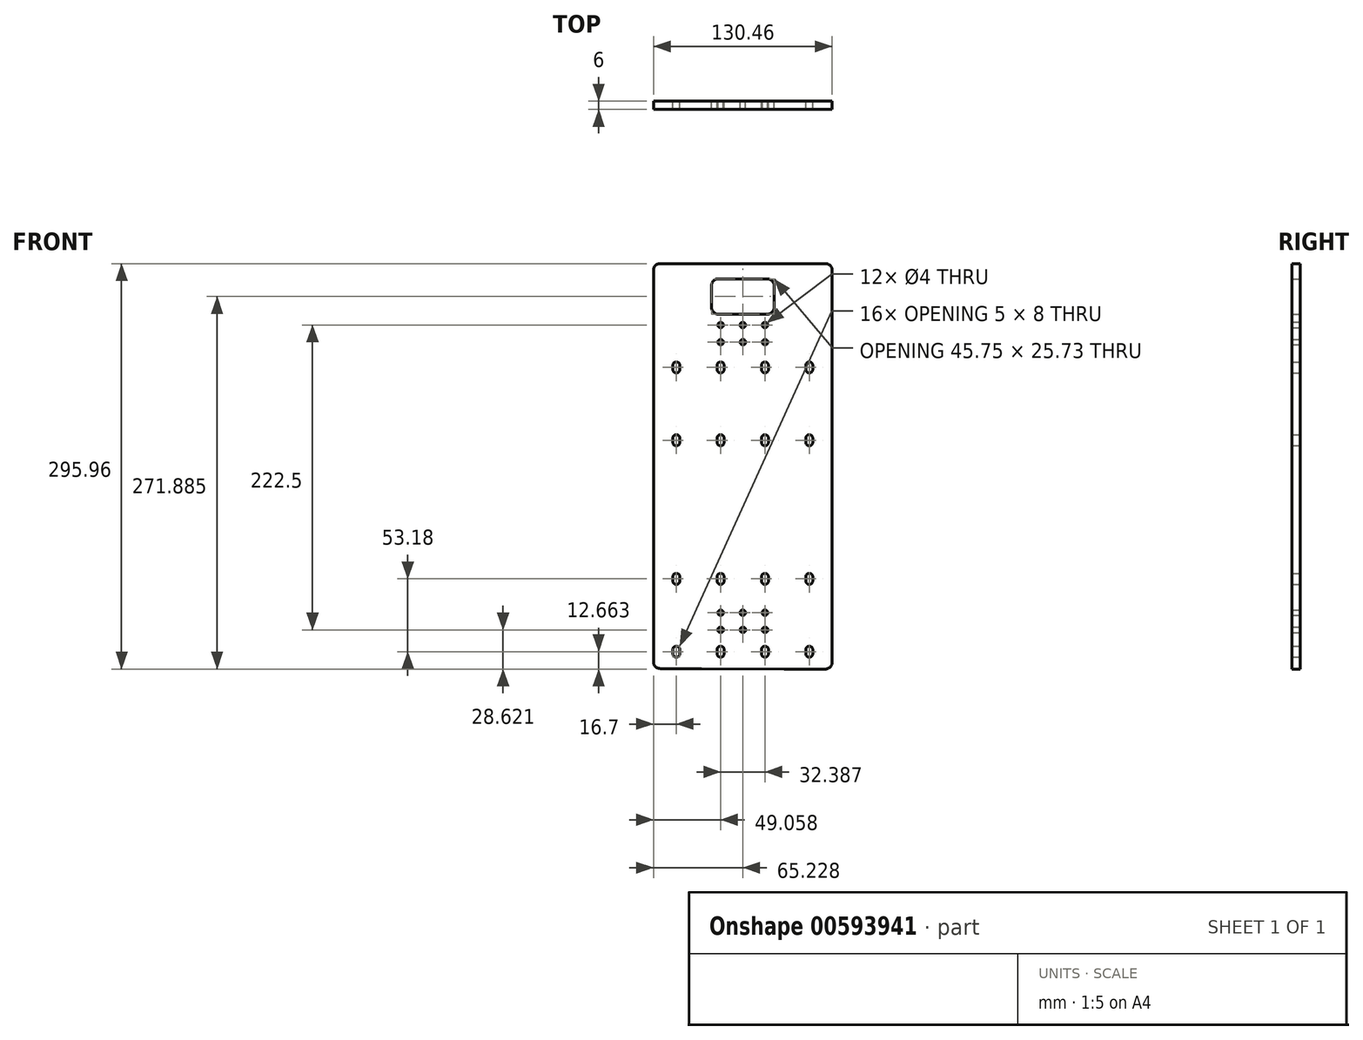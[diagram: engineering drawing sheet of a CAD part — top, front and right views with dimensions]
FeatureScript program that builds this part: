
annotation { "Feature Type Name" : "Feature", "Feature Type Description" : "" }
export const myFeature = defineFeature(function(context is Context, id is Id, definition is map)
    precondition{}
    {
        {
            var Q0;
            Q0=qCreatedBy(makeId("Front.planeOp"),FACE);
            var sketch = newSketch(context, id + "F0", { "sketchPlane" : qUnion([Q0])});
            skLineSegment(sketch, "E0.bottom", {"start": v(-82.55, 112.46) * mm, "end": v(-203.01, 112.46) * mm});
            skCircle(sketch, "E1", {"center": v(-142.78, 106.21) * mm, "radius": 2 * mm});
            skPoint(sketch, "E1.centerSnap0", {"position": v(-142.78, 112.46) * mm});
            skPoint(sketch, "E1.centerSnap1", {"position": v(-97.78, 99.96) * mm});
            skCircle(sketch, "E2.1.0.0", {"center": v(-126.61, 106.21) * mm, "radius": 2 * mm});
            skLineSegment(sketch, "E2.direction1", {"start": v(-142.78, 106.21) * mm, "end": v(-126.61, 106.21) * mm, "construction": true});
            skCircle(sketch, "E3.1.0.0", {"center": v(-158.95, 106.21) * mm, "radius": 2 * mm});
            skLineSegment(sketch, "E3.direction1", {"start": v(-142.78, 106.21) * mm, "end": v(-158.95, 106.21) * mm, "construction": true});
            skPoint(sketch, "E4", {"position": v(-97.78, 112.46) * mm});
            skCircle(sketch, "E5.2.1.0", {"center": v(-126.56, 93.71) * mm, "radius": 2 * mm});
            skCircle(sketch, "E5.2.1.1", {"center": v(-142.73, 93.71) * mm, "radius": 2 * mm});
            skCircle(sketch, "E5.2.1.2", {"center": v(-158.95, 93.71) * mm, "radius": 2 * mm});
            skLineSegment(sketch, "E5.direction1", {"start": v(-149.11, 106.21) * mm, "end": v(-149.11, 106.21) * mm});
            skLineSegment(sketch, "E5.direction2", {"start": v(-126.61, 106.21) * mm, "end": v(-126.56, 93.71) * mm, "construction": true});
            skLineSegment(sketch, "E6.bottom", {"start": v(-94.18, 79.25) * mm, "end": v(-94.4, 79.25) * mm});
            skLineSegment(sketch, "E6.top", {"start": v(-94.18, 71.25) * mm, "end": v(-94.4, 71.25) * mm});
            skLineSegment(sketch, "E6.left", {"start": v(-91.8, 76.87) * mm, "end": v(-91.8, 73.64) * mm});
            skLineSegment(sketch, "E6.right", {"start": v(-96.8, 76.87) * mm, "end": v(-96.8, 73.64) * mm});
            skPoint(sketch, "E7.visualSharp", {"position": v(-91.8, 79.25) * mm});
            skArc(sketch, "E7.filletArc", {"start": v(-91.8, 76.87) * mm, "mid": v(-92.49, 78.55) * mm, "end": v(-94.18, 79.25) * mm});
            skPoint(sketch, "E8.visualSharp", {"position": v(-91.8, 71.25) * mm});
            skArc(sketch, "E8.filletArc", {"start": v(-94.18, 71.25) * mm, "mid": v(-92.49, 71.95) * mm, "end": v(-91.8, 73.64) * mm});
            skPoint(sketch, "E9.visualSharp", {"position": v(-96.8, 71.25) * mm});
            skArc(sketch, "E9.filletArc", {"start": v(-96.8, 73.64) * mm, "mid": v(-96.1, 71.95) * mm, "end": v(-94.4, 71.25) * mm});
            skPoint(sketch, "E10.visualSharp", {"position": v(-96.8, 79.25) * mm});
            skArc(sketch, "E10.filletArc", {"start": v(-94.4, 79.25) * mm, "mid": v(-96.1, 78.55) * mm, "end": v(-96.8, 76.87) * mm});
            skPoint(sketch, "E11.0.1.0", {"position": v(-91.8, 26.07) * mm});
            skArc(sketch, "E11.0.1.1", {"start": v(-96.8, 20.46) * mm, "mid": v(-96.1, 18.77) * mm, "end": v(-94.4, 18.07) * mm});
            skArc(sketch, "E11.0.1.2", {"start": v(-91.8, 23.69) * mm, "mid": v(-92.49, 25.37) * mm, "end": v(-94.18, 26.07) * mm});
            skArc(sketch, "E11.0.1.3", {"start": v(-94.4, 26.07) * mm, "mid": v(-96.1, 25.37) * mm, "end": v(-96.8, 23.69) * mm});
            skPoint(sketch, "E11.0.1.4", {"position": v(-91.8, 18.07) * mm});
            skPoint(sketch, "E11.0.1.5", {"position": v(-96.8, 18.07) * mm});
            skLineSegment(sketch, "E11.0.1.6", {"start": v(-96.8, 23.69) * mm, "end": v(-96.8, 20.46) * mm});
            skArc(sketch, "E11.0.1.7", {"start": v(-94.18, 18.07) * mm, "mid": v(-92.49, 18.77) * mm, "end": v(-91.8, 20.46) * mm});
            skPoint(sketch, "E11.0.1.8", {"position": v(-96.8, 26.07) * mm});
            skLineSegment(sketch, "E11.0.1.9", {"start": v(-91.8, 23.69) * mm, "end": v(-91.8, 20.46) * mm});
            skLineSegment(sketch, "E11.0.1.10", {"start": v(-94.18, 18.07) * mm, "end": v(-94.4, 18.07) * mm});
            skLineSegment(sketch, "E11.0.1.11", {"start": v(-94.18, 26.07) * mm, "end": v(-94.4, 26.07) * mm});
            skPoint(sketch, "E11.1.0.0", {"position": v(-124.13, 79.25) * mm});
            skArc(sketch, "E11.1.0.1", {"start": v(-129.13, 73.64) * mm, "mid": v(-128.43, 71.95) * mm, "end": v(-126.74, 71.25) * mm});
            skArc(sketch, "E11.1.0.2", {"start": v(-124.13, 76.87) * mm, "mid": v(-124.83, 78.55) * mm, "end": v(-126.52, 79.25) * mm});
            skArc(sketch, "E11.1.0.3", {"start": v(-126.74, 79.25) * mm, "mid": v(-128.43, 78.55) * mm, "end": v(-129.13, 76.87) * mm});
            skPoint(sketch, "E11.1.0.4", {"position": v(-124.13, 71.25) * mm});
            skPoint(sketch, "E11.1.0.5", {"position": v(-129.13, 71.25) * mm});
            skLineSegment(sketch, "E11.1.0.6", {"start": v(-129.13, 76.87) * mm, "end": v(-129.13, 73.64) * mm});
            skArc(sketch, "E11.1.0.7", {"start": v(-126.52, 71.25) * mm, "mid": v(-124.83, 71.95) * mm, "end": v(-124.13, 73.64) * mm});
            skPoint(sketch, "E11.1.0.8", {"position": v(-129.13, 79.25) * mm});
            skLineSegment(sketch, "E11.1.0.9", {"start": v(-124.13, 76.87) * mm, "end": v(-124.13, 73.64) * mm});
            skLineSegment(sketch, "E11.1.0.10", {"start": v(-126.52, 71.25) * mm, "end": v(-126.74, 71.25) * mm});
            skLineSegment(sketch, "E11.1.0.11", {"start": v(-126.52, 79.25) * mm, "end": v(-126.74, 79.25) * mm});
            skPoint(sketch, "E11.1.1.0", {"position": v(-124.13, 26.07) * mm});
            skArc(sketch, "E11.1.1.1", {"start": v(-129.13, 20.46) * mm, "mid": v(-128.43, 18.77) * mm, "end": v(-126.74, 18.07) * mm});
            skArc(sketch, "E11.1.1.2", {"start": v(-124.13, 23.69) * mm, "mid": v(-124.83, 25.37) * mm, "end": v(-126.52, 26.07) * mm});
            skArc(sketch, "E11.1.1.3", {"start": v(-126.74, 26.07) * mm, "mid": v(-128.43, 25.37) * mm, "end": v(-129.13, 23.69) * mm});
            skPoint(sketch, "E11.1.1.4", {"position": v(-124.13, 18.07) * mm});
            skPoint(sketch, "E11.1.1.5", {"position": v(-129.13, 18.07) * mm});
            skLineSegment(sketch, "E11.1.1.6", {"start": v(-129.13, 23.69) * mm, "end": v(-129.13, 20.46) * mm});
            skArc(sketch, "E11.1.1.7", {"start": v(-126.52, 18.07) * mm, "mid": v(-124.83, 18.77) * mm, "end": v(-124.13, 20.46) * mm});
            skPoint(sketch, "E11.1.1.8", {"position": v(-129.13, 26.07) * mm});
            skLineSegment(sketch, "E11.1.1.9", {"start": v(-124.13, 23.69) * mm, "end": v(-124.13, 20.46) * mm});
            skLineSegment(sketch, "E11.1.1.10", {"start": v(-126.52, 18.07) * mm, "end": v(-126.74, 18.07) * mm});
            skLineSegment(sketch, "E11.1.1.11", {"start": v(-126.52, 26.07) * mm, "end": v(-126.74, 26.07) * mm});
            skPoint(sketch, "E11.2.0.0", {"position": v(-156.47, 79.25) * mm});
            skArc(sketch, "E11.2.0.1", {"start": v(-161.47, 73.64) * mm, "mid": v(-160.77, 71.95) * mm, "end": v(-159.08, 71.25) * mm});
            skArc(sketch, "E11.2.0.2", {"start": v(-156.47, 76.87) * mm, "mid": v(-157.17, 78.55) * mm, "end": v(-158.86, 79.25) * mm});
            skArc(sketch, "E11.2.0.3", {"start": v(-159.08, 79.25) * mm, "mid": v(-160.77, 78.55) * mm, "end": v(-161.47, 76.87) * mm});
            skPoint(sketch, "E11.2.0.4", {"position": v(-156.47, 71.25) * mm});
            skPoint(sketch, "E11.2.0.5", {"position": v(-161.47, 71.25) * mm});
            skLineSegment(sketch, "E11.2.0.6", {"start": v(-161.47, 76.87) * mm, "end": v(-161.47, 73.64) * mm});
            skArc(sketch, "E11.2.0.7", {"start": v(-158.86, 71.25) * mm, "mid": v(-157.17, 71.95) * mm, "end": v(-156.47, 73.64) * mm});
            skPoint(sketch, "E11.2.0.8", {"position": v(-161.47, 79.25) * mm});
            skLineSegment(sketch, "E11.2.0.9", {"start": v(-156.47, 76.87) * mm, "end": v(-156.47, 73.64) * mm});
            skLineSegment(sketch, "E11.2.0.10", {"start": v(-158.86, 71.25) * mm, "end": v(-159.08, 71.25) * mm});
            skLineSegment(sketch, "E11.2.0.11", {"start": v(-158.86, 79.25) * mm, "end": v(-159.08, 79.25) * mm});
            skPoint(sketch, "E11.2.1.0", {"position": v(-156.47, 26.07) * mm});
            skArc(sketch, "E11.2.1.1", {"start": v(-161.47, 20.46) * mm, "mid": v(-160.77, 18.77) * mm, "end": v(-159.08, 18.07) * mm});
            skArc(sketch, "E11.2.1.2", {"start": v(-156.47, 23.69) * mm, "mid": v(-157.17, 25.37) * mm, "end": v(-158.86, 26.07) * mm});
            skArc(sketch, "E11.2.1.3", {"start": v(-159.08, 26.07) * mm, "mid": v(-160.77, 25.37) * mm, "end": v(-161.47, 23.69) * mm});
            skPoint(sketch, "E11.2.1.4", {"position": v(-156.47, 18.07) * mm});
            skPoint(sketch, "E11.2.1.5", {"position": v(-161.47, 18.07) * mm});
            skLineSegment(sketch, "E11.2.1.6", {"start": v(-161.47, 23.69) * mm, "end": v(-161.47, 20.46) * mm});
            skArc(sketch, "E11.2.1.7", {"start": v(-158.86, 18.07) * mm, "mid": v(-157.17, 18.77) * mm, "end": v(-156.47, 20.46) * mm});
            skPoint(sketch, "E11.2.1.8", {"position": v(-161.47, 26.07) * mm});
            skLineSegment(sketch, "E11.2.1.9", {"start": v(-156.47, 23.69) * mm, "end": v(-156.47, 20.46) * mm});
            skLineSegment(sketch, "E11.2.1.10", {"start": v(-158.86, 18.07) * mm, "end": v(-159.08, 18.07) * mm});
            skLineSegment(sketch, "E11.2.1.11", {"start": v(-158.86, 26.07) * mm, "end": v(-159.08, 26.07) * mm});
            skPoint(sketch, "E11.3.0.0", {"position": v(-188.81, 79.25) * mm});
            skArc(sketch, "E11.3.0.1", {"start": v(-193.81, 73.64) * mm, "mid": v(-193.11, 71.95) * mm, "end": v(-191.42, 71.25) * mm});
            skArc(sketch, "E11.3.0.2", {"start": v(-188.81, 76.87) * mm, "mid": v(-189.5, 78.55) * mm, "end": v(-191.2, 79.25) * mm});
            skArc(sketch, "E11.3.0.3", {"start": v(-191.42, 79.25) * mm, "mid": v(-193.11, 78.55) * mm, "end": v(-193.81, 76.87) * mm});
            skPoint(sketch, "E11.3.0.4", {"position": v(-188.81, 71.25) * mm});
            skPoint(sketch, "E11.3.0.5", {"position": v(-193.81, 71.25) * mm});
            skLineSegment(sketch, "E11.3.0.6", {"start": v(-193.81, 76.87) * mm, "end": v(-193.81, 73.64) * mm});
            skArc(sketch, "E11.3.0.7", {"start": v(-191.2, 71.25) * mm, "mid": v(-189.5, 71.95) * mm, "end": v(-188.81, 73.64) * mm});
            skPoint(sketch, "E11.3.0.8", {"position": v(-193.81, 79.25) * mm});
            skLineSegment(sketch, "E11.3.0.9", {"start": v(-188.81, 76.87) * mm, "end": v(-188.81, 73.64) * mm});
            skLineSegment(sketch, "E11.3.0.10", {"start": v(-191.2, 71.25) * mm, "end": v(-191.42, 71.25) * mm});
            skLineSegment(sketch, "E11.3.0.11", {"start": v(-191.2, 79.25) * mm, "end": v(-191.42, 79.25) * mm});
            skPoint(sketch, "E11.3.1.0", {"position": v(-188.81, 26.07) * mm});
            skArc(sketch, "E11.3.1.1", {"start": v(-193.81, 20.46) * mm, "mid": v(-193.11, 18.77) * mm, "end": v(-191.42, 18.07) * mm});
            skArc(sketch, "E11.3.1.2", {"start": v(-188.81, 23.69) * mm, "mid": v(-189.5, 25.37) * mm, "end": v(-191.2, 26.07) * mm});
            skArc(sketch, "E11.3.1.3", {"start": v(-191.42, 26.07) * mm, "mid": v(-193.11, 25.37) * mm, "end": v(-193.81, 23.69) * mm});
            skPoint(sketch, "E11.3.1.4", {"position": v(-188.81, 18.07) * mm});
            skPoint(sketch, "E11.3.1.5", {"position": v(-193.81, 18.07) * mm});
            skLineSegment(sketch, "E11.3.1.6", {"start": v(-193.81, 23.69) * mm, "end": v(-193.81, 20.46) * mm});
            skArc(sketch, "E11.3.1.7", {"start": v(-191.2, 18.07) * mm, "mid": v(-189.5, 18.77) * mm, "end": v(-188.81, 20.46) * mm});
            skPoint(sketch, "E11.3.1.8", {"position": v(-193.81, 26.07) * mm});
            skLineSegment(sketch, "E11.3.1.9", {"start": v(-188.81, 23.69) * mm, "end": v(-188.81, 20.46) * mm});
            skLineSegment(sketch, "E11.3.1.10", {"start": v(-191.2, 18.07) * mm, "end": v(-191.42, 18.07) * mm});
            skLineSegment(sketch, "E11.3.1.11", {"start": v(-191.2, 26.07) * mm, "end": v(-191.42, 26.07) * mm});
            skLineSegment(sketch, "E11.direction1", {"start": v(-96.8, 71.25) * mm, "end": v(-129.13, 71.25) * mm, "construction": true});
            skLineSegment(sketch, "E11.direction2", {"start": v(-96.8, 71.25) * mm, "end": v(-96.8, 18.07) * mm, "construction": true});
            skPoint(sketch, "E12.0.1.0", {"position": v(-91.8, -128.25) * mm});
            skPoint(sketch, "E12.0.1.1", {"position": v(-91.8, -136.25) * mm});
            skPoint(sketch, "E12.0.1.2", {"position": v(-161.47, -75.07) * mm});
            skLineSegment(sketch, "E12.0.1.3", {"start": v(-96.8, -83.07) * mm, "end": v(-129.13, -83.07) * mm, "construction": true});
            skPoint(sketch, "E12.0.1.4", {"position": v(-161.47, -83.07) * mm});
            skPoint(sketch, "E12.0.1.5", {"position": v(-161.47, -128.25) * mm});
            skPoint(sketch, "E12.0.1.6", {"position": v(-193.81, -83.07) * mm});
            skPoint(sketch, "E12.0.1.7", {"position": v(-188.81, -136.25) * mm});
            skPoint(sketch, "E12.0.1.8", {"position": v(-193.81, -136.25) * mm});
            skPoint(sketch, "E12.0.1.9", {"position": v(-129.13, -75.07) * mm});
            skLineSegment(sketch, "E12.0.1.10", {"start": v(-96.8, -83.07) * mm, "end": v(-96.8, -136.25) * mm, "construction": true});
            skPoint(sketch, "E12.0.1.11", {"position": v(-91.8, -75.07) * mm});
            skPoint(sketch, "E12.0.1.12", {"position": v(-124.13, -75.07) * mm});
            skPoint(sketch, "E12.0.1.13", {"position": v(-96.8, -128.25) * mm});
            skPoint(sketch, "E12.0.1.14", {"position": v(-96.8, -75.07) * mm});
            skPoint(sketch, "E12.0.1.15", {"position": v(-188.81, -128.25) * mm});
            skPoint(sketch, "E12.0.1.16", {"position": v(-129.13, -128.25) * mm});
            skPoint(sketch, "E12.0.1.17", {"position": v(-193.81, -128.25) * mm});
            skPoint(sketch, "E12.0.1.18", {"position": v(-129.13, -83.07) * mm});
            skPoint(sketch, "E12.0.1.19", {"position": v(-91.8, -83.07) * mm});
            skPoint(sketch, "E12.0.1.20", {"position": v(-161.47, -136.25) * mm});
            skPoint(sketch, "E12.0.1.21", {"position": v(-96.8, -136.25) * mm});
            skPoint(sketch, "E12.0.1.22", {"position": v(-156.47, -75.07) * mm});
            skPoint(sketch, "E12.0.1.23", {"position": v(-129.13, -136.25) * mm});
            skPoint(sketch, "E12.0.1.24", {"position": v(-156.47, -136.25) * mm});
            skPoint(sketch, "E12.0.1.25", {"position": v(-124.13, -136.25) * mm});
            skPoint(sketch, "E12.0.1.26", {"position": v(-156.47, -128.25) * mm});
            skPoint(sketch, "E12.0.1.27", {"position": v(-124.13, -83.07) * mm});
            skPoint(sketch, "E12.0.1.28", {"position": v(-124.13, -128.25) * mm});
            skPoint(sketch, "E12.0.1.29", {"position": v(-193.81, -75.07) * mm});
            skPoint(sketch, "E12.0.1.30", {"position": v(-188.81, -75.07) * mm});
            skPoint(sketch, "E12.0.1.31", {"position": v(-156.47, -83.07) * mm});
            skPoint(sketch, "E12.0.1.32", {"position": v(-188.81, -83.07) * mm});
            skPoint(sketch, "E12.0.1.33", {"position": v(-96.8, -83.07) * mm});
            skLineSegment(sketch, "E12.0.1.34", {"start": v(-158.86, -128.25) * mm, "end": v(-159.08, -128.25) * mm});
            skArc(sketch, "E12.0.1.35", {"start": v(-96.8, -133.86) * mm, "mid": v(-96.1, -135.55) * mm, "end": v(-94.4, -136.25) * mm});
            skLineSegment(sketch, "E12.0.1.36", {"start": v(-193.81, -130.63) * mm, "end": v(-193.81, -133.86) * mm});
            skArc(sketch, "E12.0.1.37", {"start": v(-193.81, -133.86) * mm, "mid": v(-193.11, -135.55) * mm, "end": v(-191.42, -136.25) * mm});
            skArc(sketch, "E12.0.1.38", {"start": v(-191.2, -136.25) * mm, "mid": v(-189.5, -135.55) * mm, "end": v(-188.81, -133.86) * mm});
            skArc(sketch, "E12.0.1.39", {"start": v(-126.74, -128.25) * mm, "mid": v(-128.43, -128.95) * mm, "end": v(-129.13, -130.63) * mm});
            skArc(sketch, "E12.0.1.40", {"start": v(-158.86, -136.25) * mm, "mid": v(-157.17, -135.55) * mm, "end": v(-156.47, -133.86) * mm});
            skArc(sketch, "E12.0.1.41", {"start": v(-91.8, -130.63) * mm, "mid": v(-92.49, -128.95) * mm, "end": v(-94.18, -128.25) * mm});
            skLineSegment(sketch, "E12.0.1.42", {"start": v(-91.8, -77.45) * mm, "end": v(-91.8, -80.68) * mm});
            skArc(sketch, "E12.0.1.43", {"start": v(-126.52, -136.25) * mm, "mid": v(-124.83, -135.55) * mm, "end": v(-124.13, -133.86) * mm});
            skArc(sketch, "E12.0.1.44", {"start": v(-159.08, -128.25) * mm, "mid": v(-160.77, -128.95) * mm, "end": v(-161.47, -130.63) * mm});
            skArc(sketch, "E12.0.1.45", {"start": v(-94.18, -136.25) * mm, "mid": v(-92.49, -135.55) * mm, "end": v(-91.8, -133.86) * mm});
            skLineSegment(sketch, "E12.0.1.46", {"start": v(-94.18, -128.25) * mm, "end": v(-94.4, -128.25) * mm});
            skLineSegment(sketch, "E12.0.1.47", {"start": v(-191.2, -128.25) * mm, "end": v(-191.42, -128.25) * mm});
            skLineSegment(sketch, "E12.0.1.48", {"start": v(-126.52, -128.25) * mm, "end": v(-126.74, -128.25) * mm});
            skArc(sketch, "E12.0.1.49", {"start": v(-129.13, -133.86) * mm, "mid": v(-128.43, -135.55) * mm, "end": v(-126.74, -136.25) * mm});
            skArc(sketch, "E12.0.1.50", {"start": v(-161.47, -133.86) * mm, "mid": v(-160.77, -135.55) * mm, "end": v(-159.08, -136.25) * mm});
            skLineSegment(sketch, "E12.0.1.51", {"start": v(-188.81, -130.63) * mm, "end": v(-188.81, -133.86) * mm});
            skLineSegment(sketch, "E12.0.1.52", {"start": v(-91.8, -130.63) * mm, "end": v(-91.8, -133.86) * mm});
            skLineSegment(sketch, "E12.0.1.53", {"start": v(-124.13, -130.63) * mm, "end": v(-124.13, -133.86) * mm});
            skArc(sketch, "E12.0.1.54", {"start": v(-159.08, -75.07) * mm, "mid": v(-160.77, -75.77) * mm, "end": v(-161.47, -77.45) * mm});
            skLineSegment(sketch, "E12.0.1.55", {"start": v(-156.47, -130.63) * mm, "end": v(-156.47, -133.86) * mm});
            skArc(sketch, "E12.0.1.56", {"start": v(-124.13, -130.63) * mm, "mid": v(-124.83, -128.95) * mm, "end": v(-126.52, -128.25) * mm});
            skArc(sketch, "E12.0.1.57", {"start": v(-126.74, -75.07) * mm, "mid": v(-128.43, -75.77) * mm, "end": v(-129.13, -77.45) * mm});
            skLineSegment(sketch, "E12.0.1.58", {"start": v(-96.8, -77.45) * mm, "end": v(-96.8, -80.68) * mm});
            skArc(sketch, "E12.0.1.59", {"start": v(-94.18, -83.07) * mm, "mid": v(-92.49, -82.37) * mm, "end": v(-91.8, -80.68) * mm});
            skArc(sketch, "E12.0.1.60", {"start": v(-156.47, -77.45) * mm, "mid": v(-157.17, -75.77) * mm, "end": v(-158.86, -75.07) * mm});
            skArc(sketch, "E12.0.1.61", {"start": v(-191.42, -75.07) * mm, "mid": v(-193.11, -75.77) * mm, "end": v(-193.81, -77.45) * mm});
            skArc(sketch, "E12.0.1.62", {"start": v(-188.81, -130.63) * mm, "mid": v(-189.5, -128.95) * mm, "end": v(-191.2, -128.25) * mm});
            skArc(sketch, "E12.0.1.63", {"start": v(-191.42, -128.25) * mm, "mid": v(-193.11, -128.95) * mm, "end": v(-193.81, -130.63) * mm});
            skArc(sketch, "E12.0.1.64", {"start": v(-91.8, -77.45) * mm, "mid": v(-92.49, -75.77) * mm, "end": v(-94.18, -75.07) * mm});
            skLineSegment(sketch, "E12.0.1.65", {"start": v(-96.8, -130.63) * mm, "end": v(-96.8, -133.86) * mm});
            skArc(sketch, "E12.0.1.66", {"start": v(-96.8, -80.68) * mm, "mid": v(-96.1, -82.37) * mm, "end": v(-94.4, -83.07) * mm});
            skArc(sketch, "E12.0.1.67", {"start": v(-156.47, -130.63) * mm, "mid": v(-157.17, -128.95) * mm, "end": v(-158.86, -128.25) * mm});
            skLineSegment(sketch, "E12.0.1.68", {"start": v(-129.13, -130.63) * mm, "end": v(-129.13, -133.86) * mm});
            skLineSegment(sketch, "E12.0.1.69", {"start": v(-161.47, -130.63) * mm, "end": v(-161.47, -133.86) * mm});
            skArc(sketch, "E12.0.1.70", {"start": v(-94.4, -128.25) * mm, "mid": v(-96.1, -128.95) * mm, "end": v(-96.8, -130.63) * mm});
            skLineSegment(sketch, "E12.0.1.71", {"start": v(-191.2, -75.07) * mm, "end": v(-191.42, -75.07) * mm});
            skLineSegment(sketch, "E12.0.1.72", {"start": v(-158.86, -75.07) * mm, "end": v(-159.08, -75.07) * mm});
            skArc(sketch, "E12.0.1.73", {"start": v(-94.4, -75.07) * mm, "mid": v(-96.1, -75.77) * mm, "end": v(-96.8, -77.45) * mm});
            skArc(sketch, "E12.0.1.74", {"start": v(-124.13, -77.45) * mm, "mid": v(-124.83, -75.77) * mm, "end": v(-126.52, -75.07) * mm});
            skLineSegment(sketch, "E12.0.1.75", {"start": v(-126.52, -75.07) * mm, "end": v(-126.74, -75.07) * mm});
            skArc(sketch, "E12.0.1.76", {"start": v(-188.81, -77.45) * mm, "mid": v(-189.5, -75.77) * mm, "end": v(-191.2, -75.07) * mm});
            skLineSegment(sketch, "E12.0.1.77", {"start": v(-126.52, -83.07) * mm, "end": v(-126.74, -83.07) * mm});
            skArc(sketch, "E12.0.1.78", {"start": v(-126.52, -83.07) * mm, "mid": v(-124.83, -82.37) * mm, "end": v(-124.13, -80.68) * mm});
            skArc(sketch, "E12.0.1.79", {"start": v(-158.86, -83.07) * mm, "mid": v(-157.17, -82.37) * mm, "end": v(-156.47, -80.68) * mm});
            skLineSegment(sketch, "E12.0.1.80", {"start": v(-94.18, -75.07) * mm, "end": v(-94.4, -75.07) * mm});
            skArc(sketch, "E12.0.1.81", {"start": v(-161.47, -80.68) * mm, "mid": v(-160.77, -82.37) * mm, "end": v(-159.08, -83.07) * mm});
            skLineSegment(sketch, "E12.0.1.82", {"start": v(-161.47, -77.45) * mm, "end": v(-161.47, -80.68) * mm});
            skArc(sketch, "E12.0.1.83", {"start": v(-193.81, -80.68) * mm, "mid": v(-193.11, -82.37) * mm, "end": v(-191.42, -83.07) * mm});
            skArc(sketch, "E12.0.1.84", {"start": v(-129.13, -80.68) * mm, "mid": v(-128.43, -82.37) * mm, "end": v(-126.74, -83.07) * mm});
            skLineSegment(sketch, "E12.0.1.85", {"start": v(-94.18, -136.25) * mm, "end": v(-94.4, -136.25) * mm});
            skLineSegment(sketch, "E12.0.1.86", {"start": v(-129.13, -77.45) * mm, "end": v(-129.13, -80.68) * mm});
            skLineSegment(sketch, "E12.0.1.87", {"start": v(-193.81, -77.45) * mm, "end": v(-193.81, -80.68) * mm});
            skLineSegment(sketch, "E12.0.1.88", {"start": v(-188.81, -77.45) * mm, "end": v(-188.81, -80.68) * mm});
            skLineSegment(sketch, "E12.0.1.89", {"start": v(-156.47, -77.45) * mm, "end": v(-156.47, -80.68) * mm});
            skLineSegment(sketch, "E12.0.1.90", {"start": v(-158.86, -83.07) * mm, "end": v(-159.08, -83.07) * mm});
            skArc(sketch, "E12.0.1.91", {"start": v(-191.2, -83.07) * mm, "mid": v(-189.5, -82.37) * mm, "end": v(-188.81, -80.68) * mm});
            skLineSegment(sketch, "E12.0.1.92", {"start": v(-191.2, -83.07) * mm, "end": v(-191.42, -83.07) * mm});
            skLineSegment(sketch, "E12.0.1.93", {"start": v(-124.13, -77.45) * mm, "end": v(-124.13, -80.68) * mm});
            skLineSegment(sketch, "E12.0.1.94", {"start": v(-191.2, -136.25) * mm, "end": v(-191.42, -136.25) * mm});
            skLineSegment(sketch, "E12.0.1.95", {"start": v(-94.18, -83.07) * mm, "end": v(-94.4, -83.07) * mm});
            skLineSegment(sketch, "E12.0.1.96", {"start": v(-158.86, -136.25) * mm, "end": v(-159.08, -136.25) * mm});
            skLineSegment(sketch, "E12.0.1.97", {"start": v(-126.52, -136.25) * mm, "end": v(-126.74, -136.25) * mm});
            skLineSegment(sketch, "E12.direction1", {"start": v(-193.81, 18.07) * mm, "end": v(-168.81, 18.07) * mm, "construction": true});
            skLineSegment(sketch, "E12.direction2", {"start": v(-193.81, 18.07) * mm, "end": v(-193.81, -136.25) * mm, "construction": true});
            skLineSegment(sketch, "E13", {"start": v(-203.01, -144.57) * mm, "end": v(-173.01, -144.57) * mm});
            skLineSegment(sketch, "E14", {"start": v(-112.55, -144.9) * mm, "end": v(-82.55, -144.9) * mm});
            skLineSegment(sketch, "E15", {"start": v(-208.01, 107.46) * mm, "end": v(-208.01, -139.57) * mm});
            skLineSegment(sketch, "E16", {"start": v(-77.55, 107.46) * mm, "end": v(-77.55, -139.9) * mm});
            skPoint(sketch, "E17.visualSharp", {"position": v(-208.01, -144.57) * mm});
            skArc(sketch, "E17.filletArc", {"start": v(-208.01, -139.57) * mm, "mid": v(-206.55, -143.1) * mm, "end": v(-203.01, -144.57) * mm});
            skPoint(sketch, "E18.visualSharp", {"position": v(-77.55, -144.9) * mm});
            skArc(sketch, "E18.filletArc", {"start": v(-82.55, -144.9) * mm, "mid": v(-79.02, -143.44) * mm, "end": v(-77.55, -139.9) * mm});
            skPoint(sketch, "E19.visualSharp", {"position": v(-208.01, 112.46) * mm});
            skArc(sketch, "E19.filletArc", {"start": v(-203.01, 112.46) * mm, "mid": v(-206.55, 111) * mm, "end": v(-208.01, 107.46) * mm});
            skPoint(sketch, "E20.visualSharp", {"position": v(-77.55, 112.46) * mm});
            skArc(sketch, "E20.filletArc", {"start": v(-77.55, 107.46) * mm, "mid": v(-79.02, 111) * mm, "end": v(-82.55, 112.46) * mm});
            skLineSegment(sketch, "E21", {"start": v(-173.01, -144.57) * mm, "end": v(-112.55, -144.9) * mm});
            skPoint(sketch, "E22.0.1.0", {"position": v(-142.78, -97.54) * mm});
            skLineSegment(sketch, "E22.0.1.1", {"start": v(-126.61, -103.79) * mm, "end": v(-126.56, -116.29) * mm, "construction": true});
            skCircle(sketch, "E22.0.1.3", {"center": v(-158.95, -116.29) * mm, "radius": 2 * mm});
            skLineSegment(sketch, "E22.0.1.9", {"start": v(-142.78, -103.79) * mm, "end": v(-158.95, -103.79) * mm, "construction": true});
            skLineSegment(sketch, "E22.0.1.10", {"start": v(-142.78, -103.79) * mm, "end": v(-126.61, -103.79) * mm, "construction": true});
            skCircle(sketch, "E22.0.1.11", {"center": v(-142.78, -103.79) * mm, "radius": 2 * mm});
            skPoint(sketch, "E22.0.1.13", {"position": v(-142.78, -97.54) * mm});
            skCircle(sketch, "E22.0.1.15", {"center": v(-158.95, -103.79) * mm, "radius": 2 * mm});
            skCircle(sketch, "E22.0.1.16", {"center": v(-126.61, -103.79) * mm, "radius": 2 * mm});
            skCircle(sketch, "E22.0.1.18", {"center": v(-142.73, -116.29) * mm, "radius": 2 * mm});
            skCircle(sketch, "E22.0.1.19", {"center": v(-126.56, -116.29) * mm, "radius": 2 * mm});
            skLineSegment(sketch, "E22.direction1", {"start": v(-158.95, 93.71) * mm, "end": v(-133.95, 93.71) * mm, "construction": true});
            skLineSegment(sketch, "E22.direction2", {"start": v(-158.95, 93.71) * mm, "end": v(-158.95, -116.29) * mm, "construction": true});
            skLineSegment(sketch, "E23.bottom", {"start": v(-77.55, 107.46) * mm, "end": v(-208.01, 107.46) * mm});
            skLineSegment(sketch, "E23.top", {"start": v(-82.55, 151.05) * mm, "end": v(-203.01, 151.05) * mm});
            skLineSegment(sketch, "E23.left", {"start": v(-77.55, 107.46) * mm, "end": v(-77.55, 146.05) * mm});
            skLineSegment(sketch, "E23.right", {"start": v(-208.01, 107.46) * mm, "end": v(-208.01, 146.05) * mm});
            skLineSegment(sketch, "E24.bottom", {"start": v(-124.9, 114.1) * mm, "end": v(-160.66, 114.1) * mm});
            skLineSegment(sketch, "E24.top", {"start": v(-124.9, 139.84) * mm, "end": v(-160.66, 139.84) * mm});
            skLineSegment(sketch, "E24.left", {"start": v(-119.9, 119.1) * mm, "end": v(-119.9, 134.84) * mm});
            skLineSegment(sketch, "E24.right", {"start": v(-165.66, 119.1) * mm, "end": v(-165.66, 134.84) * mm});
            skPoint(sketch, "E24.middle", {"position": v(-142.78, 126.98) * mm});
            skPoint(sketch, "E25.visualSharp", {"position": v(-165.66, 139.84) * mm});
            skArc(sketch, "E25.filletArc", {"start": v(-160.66, 139.84) * mm, "mid": v(-164.2, 138.38) * mm, "end": v(-165.66, 134.84) * mm});
            skPoint(sketch, "E26.visualSharp", {"position": v(-165.66, 114.1) * mm});
            skArc(sketch, "E26.filletArc", {"start": v(-165.66, 119.1) * mm, "mid": v(-164.2, 115.57) * mm, "end": v(-160.66, 114.1) * mm});
            skPoint(sketch, "E27.visualSharp", {"position": v(-119.9, 114.1) * mm});
            skArc(sketch, "E27.filletArc", {"start": v(-124.9, 114.1) * mm, "mid": v(-121.37, 115.57) * mm, "end": v(-119.9, 119.1) * mm});
            skPoint(sketch, "E28.visualSharp", {"position": v(-119.9, 139.84) * mm});
            skArc(sketch, "E28.filletArc", {"start": v(-119.9, 134.84) * mm, "mid": v(-121.37, 138.38) * mm, "end": v(-124.9, 139.84) * mm});
            skPoint(sketch, "E29.visualSharp", {"position": v(-208.01, 151.05) * mm});
            skArc(sketch, "E29.filletArc", {"start": v(-203.01, 151.05) * mm, "mid": v(-206.55, 149.6) * mm, "end": v(-208.01, 146.05) * mm});
            skPoint(sketch, "E30.visualSharp", {"position": v(-77.55, 151.05) * mm});
            skArc(sketch, "E30.filletArc", {"start": v(-77.55, 146.05) * mm, "mid": v(-79.02, 149.6) * mm, "end": v(-82.55, 151.05) * mm});
            skSolve(sketch);
        }
        {
            var Q0;
            Q0=makeQuery(id+"F0.imprint","IMPRINT",FACE,{"disambiguationData":[TD([[makeQuery(id+"F0.imprint","IMPRINT",EDGE,{"derivedFrom":sQuery(id+"F0.wireOp",EDGE,"E5.2.1.0")}),-1.0]])]});
            var Q1;
            Q1=makeQuery(id+"F0.imprint","IMPRINT",FACE,{"disambiguationData":[TD([[makeQuery(id+"F0.imprint","IMPRINT",EDGE,{"derivedFrom":sQuery(id+"F0.wireOp",EDGE,"E0.bottom")}),1.0]])]});
            var Q2;
            Q2=makeQuery(id+"F0.imprint","IMPRINT",FACE,{"disambiguationData":[TD([[makeQuery(id+"F0.imprint","IMPRINT",EDGE,{"derivedFrom":sQuery(id+"F0.wireOp",EDGE,"E0.bottom")}),-1.0]])]});
            extrude(context, id + "F1", {"entities" : qUnion([Q0, Q1, Q2]), "depth" : 6 * mm, "offsetDistance" : 25 * mm});
        }
    });
